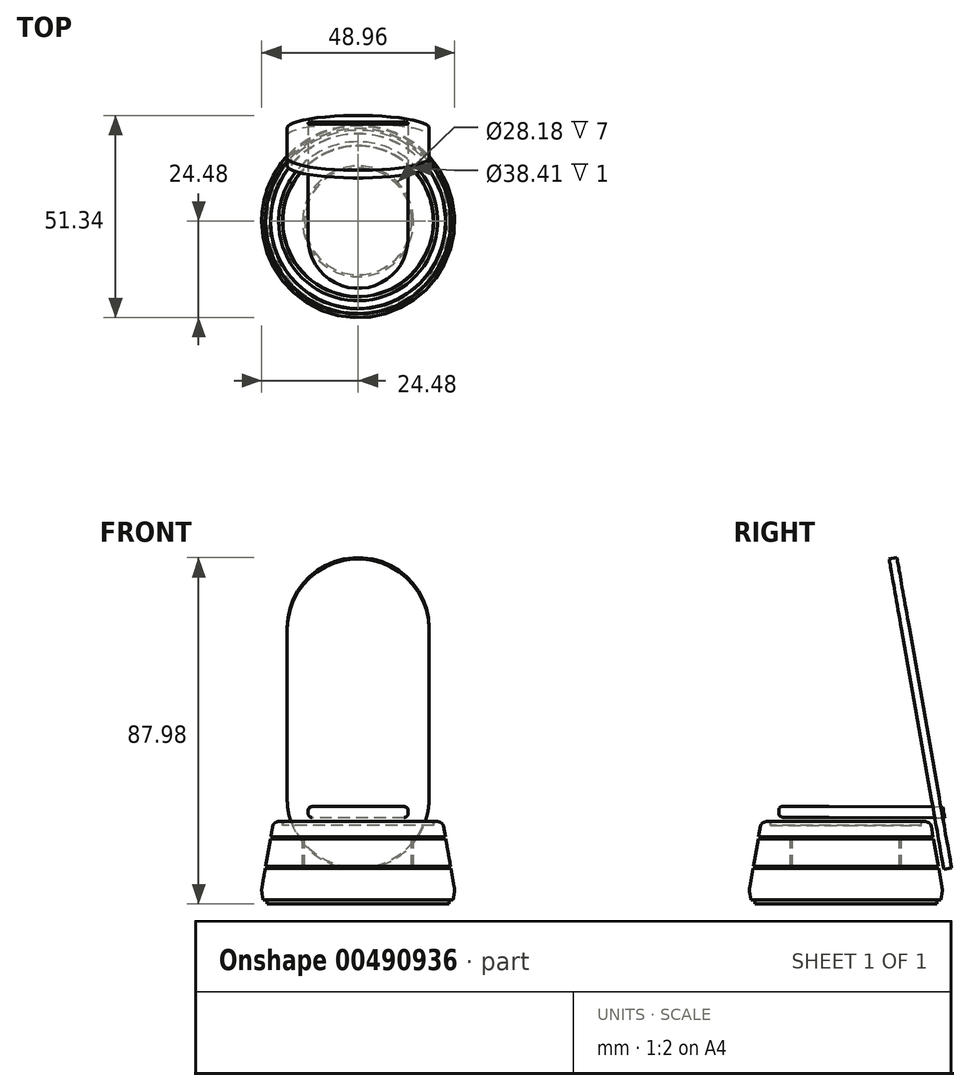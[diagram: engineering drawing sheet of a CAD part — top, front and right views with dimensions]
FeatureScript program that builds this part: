
annotation { "Feature Type Name" : "Feature", "Feature Type Description" : "" }
export const myFeature = defineFeature(function(context is Context, id is Id, definition is map)
    precondition{}
    {
        {
            var Q0;
            Q0=qCreatedBy(makeId("Right.planeOp"),FACE);
            var sketch = newSketch(context, id + "F0", { "sketchPlane" : qUnion([Q0])});
            skLineSegment(sketch, "E0", {"start": v(0, 0) * mm, "end": v(25, 0) * mm});
            skLineSegment(sketch, "E1", {"start": v(25, 0) * mm, "end": v(23.59, 8) * mm});
            skLineSegment(sketch, "E2", {"start": v(23.59, 8) * mm, "end": v(13.59, 8) * mm});
            skLineSegment(sketch, "E3", {"start": v(13.59, 8) * mm, "end": v(13.59, 16) * mm});
            skLineSegment(sketch, "E4", {"start": v(13.59, 16) * mm, "end": v(22.18, 16) * mm});
            skLineSegment(sketch, "E5", {"start": v(22.18, 16) * mm, "end": v(21.47, 20) * mm});
            skLineSegment(sketch, "E6", {"start": v(21.47, 20) * mm, "end": v(0, 20) * mm});
            skLineSegment(sketch, "E7", {"start": v(0, 20) * mm, "end": v(0, 0) * mm});
            skLineSegment(sketch, "E8", {"start": v(21.47, 20) * mm, "end": v(25, 0) * mm, "construction": true});
            skLineSegment(sketch, "E9", {"start": v(22.27, 15.5) * mm, "end": v(14.09, 15.5) * mm});
            skLineSegment(sketch, "E10", {"start": v(14.09, 15.5) * mm, "end": v(14.09, 8.5) * mm});
            skLineSegment(sketch, "E11", {"start": v(14.09, 8.5) * mm, "end": v(23.5, 8.5) * mm});
            skLineSegment(sketch, "E12", {"start": v(23.5, 8.5) * mm, "end": v(22.27, 15.5) * mm});
            skLineSegment(sketch, "E13", {"start": v(22.45, 26) * mm, "end": v(8.55, 104.78) * mm, "construction": true});
            skLineSegment(sketch, "E14", {"start": v(22.45, 26) * mm, "end": v(22.45, 40.65) * mm, "construction": true});
            skSolve(sketch);
        }
        {
            var Q0;
            Q0=makeQuery(id+"F0.imprint","IMPRINT",FACE,{"disambiguationData":[TD([[makeQuery(id+"F0.imprint","IMPRINT",EDGE,{"derivedFrom":sQuery(id+"F0.wireOp",EDGE,"E0")}),1.0]])]});
            var Q1;
            Q1=makeQuery(id+"F0.imprint","IMPRINT",FACE,{"disambiguationData":[TD([[makeQuery(id+"F0.imprint","IMPRINT",EDGE,{"derivedFrom":sQuery(id+"F0.wireOp",EDGE,"E9")}),1.0]])]});
            var Q2;
            Q2=sQuery(id+"F0.wireOp",EDGE,"E7");
            revolve(context, id + "F1", {"entities" : qUnion([Q0, Q1]), "axis" : qUnion([Q2]), "revolveType" : RevolveType.FULL});
        }
        {
            var Q0;
            Q0=makeQuery(id+"F1.opRevolve","SWEPT_EDGE",EDGE,{"disambiguationData":[OSD([sQuery(id+"F0.wireOp",EDGE,"E0"),sQuery(id+"F0.wireOp",EDGE,"E1")])]});
            chamfer(context, id + "F2", {"entities" : qUnion([Q0]), "chamferType" : ChamferType.OFFSET_ANGLE, "width" : 2.54 * mm, "oppositeDirection" : false, "angle" : 20 * degree, "tangentPropagation" : true});
        }
        {
            var Q0;
            Q0=makeQuery(id+"F1.opRevolve","SWEPT_EDGE",EDGE,{"disambiguationData":[OSD([sQuery(id+"F0.wireOp",EDGE,"E5"),sQuery(id+"F0.wireOp",EDGE,"E6")])]});
            chamfer(context, id + "F3", {"entities" : qUnion([Q0]), "chamferType" : ChamferType.OFFSET_ANGLE, "width" : 1.27 * mm, "oppositeDirection" : false, "angle" : 20 * degree, "tangentPropagation" : true});
        }
        {
            var Q0;
            {var subQ0=sQuery(id+"F0.wireOp",EDGE,"E5");Q0=makeQuery(id+"F3.opChamfer","BLEND_EDGE",EDGE,{"blendedFrom":[makeQuery(id+"F1.opRevolve","SWEPT_EDGE",EDGE,{"disambiguationData":[OSD([subQ0,sQuery(id+"F0.wireOp",EDGE,"E6")])]}),makeQuery(id+"F1.opRevolve","SWEPT_FACE",FACE,{"disambiguationData":[OSD([subQ0])]})],"blendedInto":[makeQuery(id+"F1.opRevolve","SWEPT_FACE",FACE,{"disambiguationData":[OSD([subQ0])]})]});}
            fillet(context, id + "F4", {"entities" : qUnion([Q0]), "radius" : 1.27 * mm, "tangentPropagation" : true, "allowEdgeOverflow" : false});
        }
        {
            var Q0;
            {var subQ0=sQuery(id+"F0.wireOp",EDGE,"E1");Q0=makeQuery(id+"F2.opChamfer","BLEND_EDGE",EDGE,{"blendedFrom":[makeQuery(id+"F1.opRevolve","SWEPT_EDGE",EDGE,{"disambiguationData":[OSD([sQuery(id+"F0.wireOp",EDGE,"E0"),subQ0])]}),makeQuery(id+"F1.opRevolve","SWEPT_FACE",FACE,{"disambiguationData":[OSD([subQ0])]})],"blendedInto":[makeQuery(id+"F1.opRevolve","SWEPT_FACE",FACE,{"disambiguationData":[OSD([subQ0])]})]});}
            fillet(context, id + "F5", {"entities" : qUnion([Q0]), "radius" : 5.08 * mm, "tangentPropagation" : true, "allowEdgeOverflow" : false});
        }
        {
            var Q0;
            Q0=makeQuery(id+"F1.opRevolve","SWEPT_FACE",FACE,{"disambiguationData":[OSD([sQuery(id+"F0.wireOp",EDGE,"E0")])]});
            var sketch = newSketch(context, id + "F6", { "sketchPlane" : qUnion([Q0])});
            skCircle(sketch, "E15.0", {"center": v(0, 0) * mm, "radius": 23.12 * mm});
            skSolve(sketch);
        }
        {
            var Q0;
            Q0=qSketchRegion(id+"F6",true);
            extrude(context, id + "F7", {"entities" : qUnion([Q0]), "depth" : 1 * mm});
        }
        {
            var Q0;
            Q0=makeQuery(id+"F1.opRevolve","SWEPT_FACE",FACE,{"disambiguationData":[OSD([sQuery(id+"F0.wireOp",EDGE,"E6")])]});
            var sketch = newSketch(context, id + "F8", { "sketchPlane" : qUnion([Q0])});
            skCircle(sketch, "E16.0", {"center": v(0, 0) * mm, "radius": 19.2 * mm});
            skSolve(sketch);
        }
        {
            var Q0;
            Q0=qSketchRegion(id+"F8",true);
            extrude(context, id + "F9", {"entities" : qUnion([Q0]), "operationType" : NewBodyOperationType.REMOVE, "oppositeDirection" : true, "depth" : 1 * mm});
        }
        {
            var Q0;
            Q0=makeQuery(id+"F9.boolean.opBoolean","COPY",FACE,{"derivedFrom":makeQuery(id+"F9.opExtrude","CAP_FACE",FACE,{"disambiguationData":[OSD([sQuery(id+"F8.wireOp",EDGE,"E16.0")])],"isStart":false})});
            var sketch = newSketch(context, id + "F10", { "sketchPlane" : qUnion([Q0])});
            skCircle(sketch, "E17.0", {"center": v(0, 0) * mm, "radius": 19.1 * mm});
            skSolve(sketch);
        }
        {
            var Q0;
            Q0=qSketchRegion(id+"F10",true);
            extrude(context, id + "F11", {"entities" : qUnion([Q0]), "depth" : 1 * mm});
        }
        {
            var Q0;
            Q0=qCreatedBy(makeId("Right.planeOp"),FACE);
            var sketch = newSketch(context, id + "F12", { "sketchPlane" : qUnion([Q0])});
            skLineSegment(sketch, "E18", {"start": v(24.89, 7.85) * mm, "end": v(11, 86.64) * mm});
            skLineSegment(sketch, "E19.0", {"start": v(26.86, 8.2) * mm, "end": v(12.97, 86.98) * mm});
            skLineSegment(sketch, "E20", {"start": v(12.97, 86.98) * mm, "end": v(11, 86.64) * mm});
            skLineSegment(sketch, "E21", {"start": v(26.86, 8.2) * mm, "end": v(24.89, 7.85) * mm});
            skSolve(sketch);
        }
        {
            var Q0;
            Q0=makeQuery(id+"F12.imprint","IMPRINT",FACE,{"disambiguationData":[TD([[makeQuery(id+"F12.imprint","IMPRINT",EDGE,{"derivedFrom":sQuery(id+"F12.wireOp",EDGE,"E18")}),-1.0]])]});
            extrude(context, id + "F13", {"entities" : qUnion([Q0]), "endBound" : BoundingType.SYMMETRIC, "depth" : 36 * mm});
        }
        {
            var Q0;
            Q0=makeQuery(id+"F13.opExtrude","CAP_EDGE",EDGE,{"disambiguationData":[OSD([sQuery(id+"F12.wireOp",EDGE,"E20")])],"isStart":false});
            var Q1;
            Q1=makeQuery(id+"F13.opExtrude","CAP_EDGE",EDGE,{"disambiguationData":[OSD([sQuery(id+"F12.wireOp",EDGE,"E20")])],"isStart":true});
            var Q2;
            Q2=makeQuery(id+"F13.opExtrude","CAP_EDGE",EDGE,{"disambiguationData":[OSD([sQuery(id+"F12.wireOp",EDGE,"E21")])],"isStart":false});
            var Q3;
            Q3=makeQuery(id+"F13.opExtrude","CAP_EDGE",EDGE,{"disambiguationData":[OSD([sQuery(id+"F12.wireOp",EDGE,"E21")])],"isStart":true});
            fillet(context, id + "F14", {"entities" : qUnion([Q0, Q1, Q2, Q3]), "radius" : 18 * mm, "tangentPropagation" : true, "allowEdgeOverflow" : false});
        }
        {
            var Q0;
            Q0=qCreatedBy(makeId("Right.planeOp"),FACE);
            var sketch = newSketch(context, id + "F15", { "sketchPlane" : qUnion([Q0])});
            skLineSegment(sketch, "E22.0", {"start": v(24.22, 26.01) * mm, "end": v(27.35, 8.29) * mm, "construction": true});
            skLineSegment(sketch, "E23", {"start": v(24.65, 23.6) * mm, "end": v(-17.04, 23.81) * mm});
            skLineSegment(sketch, "E24", {"start": v(-17.04, 23.81) * mm, "end": v(-17.05, 21.06) * mm});
            skLineSegment(sketch, "E25", {"start": v(-17.05, 21.06) * mm, "end": v(25.14, 20.84) * mm});
            skLineSegment(sketch, "E26", {"start": v(24.65, 23.6) * mm, "end": v(25.14, 20.84) * mm});
            skSolve(sketch);
        }
        {
            var Q0;
            Q0=makeQuery(id+"F15.imprint","IMPRINT",FACE,{"disambiguationData":[TD([[makeQuery(id+"F15.imprint","IMPRINT",EDGE,{"derivedFrom":sQuery(id+"F15.wireOp",EDGE,"E23")}),1.0]])]});
            extrude(context, id + "F16", {"entities" : qUnion([Q0]), "endBound" : BoundingType.SYMMETRIC, "depth" : 25.4 * mm});
        }
        {
            var Q0;
            Q0=makeQuery(id+"F16.opExtrude","CAP_EDGE",EDGE,{"disambiguationData":[OSD([sQuery(id+"F15.wireOp",EDGE,"E24")])],"isStart":true});
            var Q1;
            Q1=makeQuery(id+"F16.opExtrude","CAP_EDGE",EDGE,{"disambiguationData":[OSD([sQuery(id+"F15.wireOp",EDGE,"E24")])],"isStart":false});
            fillet(context, id + "F17", {"entities" : qUnion([Q0, Q1]), "radius" : 12.7 * mm, "tangentPropagation" : true, "allowEdgeOverflow" : false});
        }
        {
            var Q0;
            Q0=makeQuery(id+"F16.opExtrude","CAP_EDGE",EDGE,{"disambiguationData":[OSD([sQuery(id+"F15.wireOp",EDGE,"E25")])],"isStart":false});
            var Q1;
            Q1=makeQuery(id+"F16.opExtrude","CAP_EDGE",EDGE,{"disambiguationData":[OSD([sQuery(id+"F15.wireOp",EDGE,"E23")])],"isStart":false});
            fillet(context, id + "F18", {"entities" : qUnion([Q0, Q1]), "radius" : 1 * mm, "tangentPropagation" : true, "allowEdgeOverflow" : false});
        }
    });
